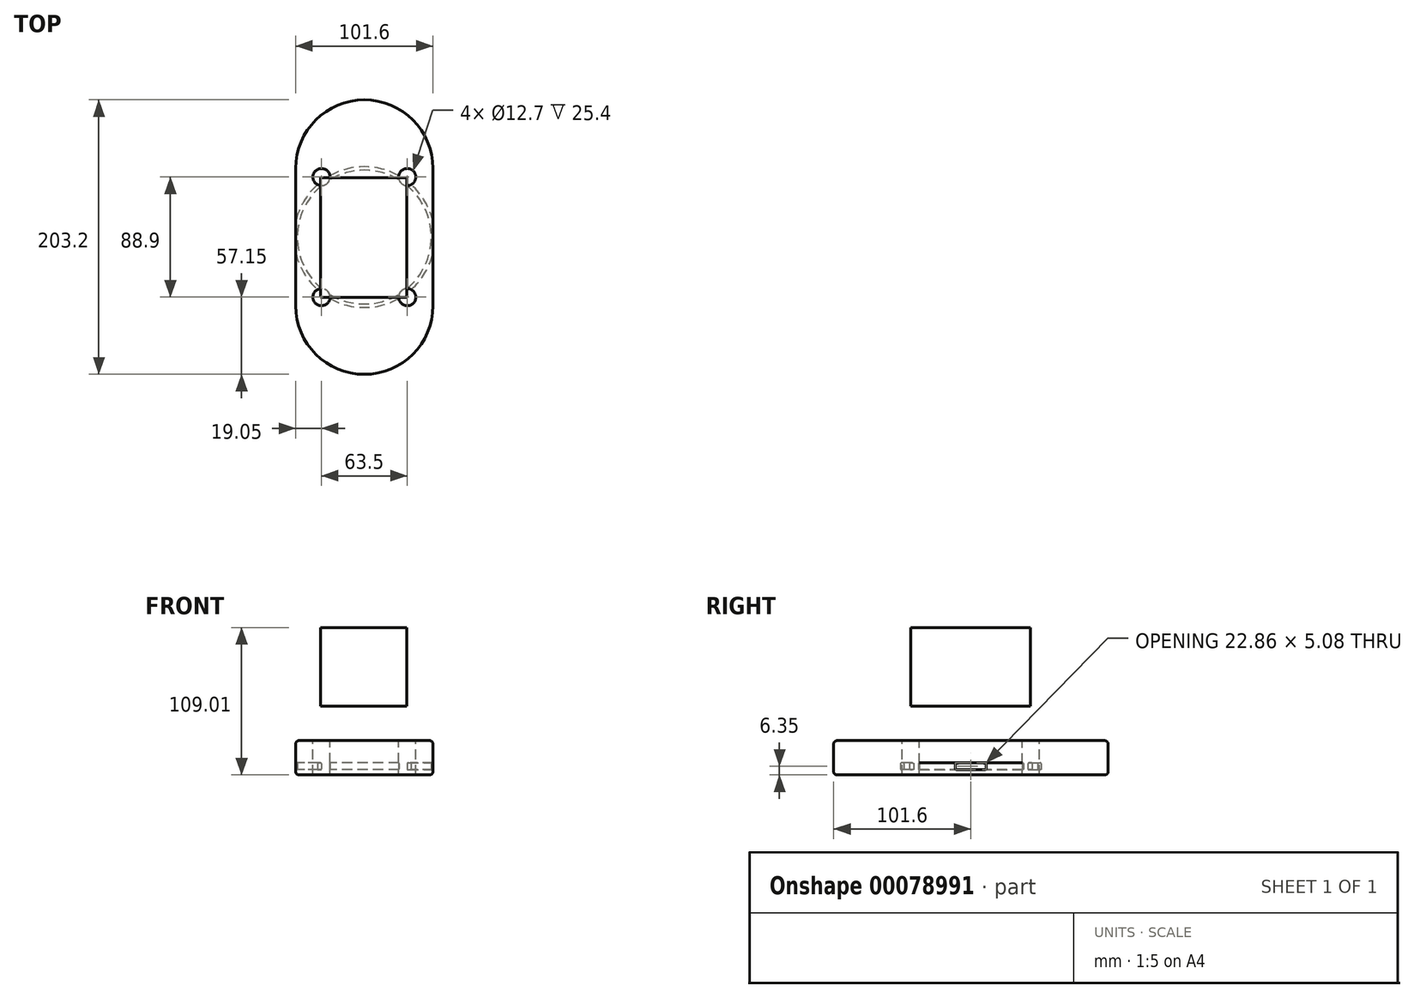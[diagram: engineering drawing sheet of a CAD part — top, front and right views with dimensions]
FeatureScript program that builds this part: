
annotation { "Feature Type Name" : "Feature", "Feature Type Description" : "" }
export const myFeature = defineFeature(function(context is Context, id is Id, definition is map)
    precondition{}
    {
        {
            var Q0;
            Q0=qCreatedBy(makeId("Top.planeOp"),FACE);
            var sketch = newSketch(context, id + "F0", { "sketchPlane" : qUnion([Q0])});
            skLineSegment(sketch, "E0", {"start": v(-50.8, -50.8) * mm, "end": v(-50.8, 50.8) * mm});
            skArc(sketch, "E1", {"start": v(50.8, 50.8) * mm, "mid": v(0, 101.6) * mm, "end": v(-50.8, 50.8) * mm});
            skArc(sketch, "E2", {"start": v(-50.8, -50.8) * mm, "mid": v(0, -101.6) * mm, "end": v(50.8, -50.8) * mm});
            skLineSegment(sketch, "E3", {"start": v(50.8, 50.8) * mm, "end": v(50.8, -50.8) * mm});
            skLineSegment(sketch, "E4", {"start": v(0, 50.8) * mm, "end": v(0, -50.8) * mm, "construction": true});
            skSolve(sketch);
        }
        {
            var Q0;
            Q0=qCreatedBy(makeId("Front.planeOp"),FACE);
            var sketch = newSketch(context, id + "F1", { "sketchPlane" : qUnion([Q0])});
            skLineSegment(sketch, "E5.bottom", {"start": v(51.44, 3.81) * mm, "end": v(50.16, 3.81) * mm});
            skLineSegment(sketch, "E5.top", {"start": v(51.44, 8.89) * mm, "end": v(50.16, 8.89) * mm});
            skLineSegment(sketch, "E5.left", {"start": v(52.07, 4.45) * mm, "end": v(52.07, 8.25) * mm});
            skLineSegment(sketch, "E5.right", {"start": v(49.53, 4.45) * mm, "end": v(49.53, 8.25) * mm});
            skLineSegment(sketch, "E6", {"start": v(50.8, 3.81) * mm, "end": v(50.8, 8.89) * mm, "construction": true});
            skLineSegment(sketch, "E7", {"start": v(52.07, 6.35) * mm, "end": v(49.53, 6.35) * mm, "construction": true});
            skPoint(sketch, "E8.visualSharp", {"position": v(52.07, 8.89) * mm});
            skArc(sketch, "E8.filletArc", {"start": v(52.07, 8.25) * mm, "mid": v(51.88, 8.7) * mm, "end": v(51.44, 8.89) * mm});
            skPoint(sketch, "E9.visualSharp", {"position": v(49.53, 8.9) * mm});
            skArc(sketch, "E9.filletArc", {"start": v(50.16, 8.89) * mm, "mid": v(49.72, 8.7) * mm, "end": v(49.53, 8.25) * mm});
            skPoint(sketch, "E10.visualSharp", {"position": v(49.53, 3.81) * mm});
            skArc(sketch, "E10.filletArc", {"start": v(49.53, 4.45) * mm, "mid": v(49.72, 4) * mm, "end": v(50.16, 3.81) * mm});
            skPoint(sketch, "E11.visualSharp", {"position": v(52.07, 3.81) * mm});
            skArc(sketch, "E11.filletArc", {"start": v(51.44, 3.81) * mm, "mid": v(51.88, 4) * mm, "end": v(52.07, 4.45) * mm});
            skSolve(sketch);
        }
        {
            var Q0;
            Q0 = qSketchRegion(id + "F0", true);
            extrude(context, id + "F2", {"entities" : qUnion([Q0]), "depth" : 25.4 * mm});
        }
        {
            var Q0;
            Q0=makeQuery(id+"F2.opExtrude","CAP_FACE",FACE,{"disambiguationData":[OSD([sQuery(id+"F0.wireOp",EDGE,"E0"),sQuery(id+"F0.wireOp",EDGE,"E1"),sQuery(id+"F0.wireOp",EDGE,"E2"),sQuery(id+"F0.wireOp",EDGE,"E3")])],"isStart":false});
            var sketch = newSketch(context, id + "F3", { "sketchPlane" : qUnion([Q0])});
            skLineSegment(sketch, "E12.bottom", {"start": v(-31.75, 44.45) * mm, "end": v(31.75, 44.45) * mm, "construction": true});
            skLineSegment(sketch, "E12.top", {"start": v(-31.75, -44.45) * mm, "end": v(31.75, -44.45) * mm, "construction": true});
            skLineSegment(sketch, "E12.left", {"start": v(-31.75, 44.45) * mm, "end": v(-31.75, -44.45) * mm, "construction": true});
            skLineSegment(sketch, "E12.right", {"start": v(31.75, 44.45) * mm, "end": v(31.75, -44.45) * mm, "construction": true});
            skCircle(sketch, "E13", {"center": v(-31.75, 44.45) * mm, "radius": 6.35 * mm});
            skCircle(sketch, "E14", {"center": v(31.75, 44.45) * mm, "radius": 6.35 * mm});
            skCircle(sketch, "E15", {"center": v(31.75, -44.45) * mm, "radius": 6.35 * mm});
            skCircle(sketch, "E16", {"center": v(-31.75, -44.45) * mm, "radius": 6.35 * mm});
            skSolve(sketch);
        }
        {
            var Q0;
            Q0 = qSketchRegion(id + "F3", true);
            extrude(context, id + "F4", {"entities" : qUnion([Q0]), "operationType" : NewBodyOperationType.REMOVE, "oppositeDirection" : true, "depth" : 25.4 * mm});
        }
        {
            var Q0;
            Q0=qCreatedBy(makeId("Front.planeOp"),FACE);
            var sketch = newSketch(context, id + "F5", { "sketchPlane" : qUnion([Q0])});
            skLineSegment(sketch, "E17", {"start": v(0, 58.33) * mm, "end": v(0, -58.9) * mm});
            skSolve(sketch);
        }
        {
            var Q0;
            Q0=makeQuery(id+"F1.imprint","IMPRINT",FACE,{"disambiguationData":[TD([[makeQuery(id+"F1.imprint","IMPRINT",EDGE,{"derivedFrom":sQuery(id+"F1.wireOp",EDGE,"E5.bottom")}),-1.0]])]});
            var Q1;
            Q1=sQuery(id+"F5.wireOp",EDGE,"E17");
            revolve(context, id + "F6", {"operationType" : NewBodyOperationType.REMOVE, "entities" : qUnion([Q0]), "axis" : qUnion([Q1]), "revolveType" : RevolveType.FULL, "oppositeDirection" : true});
        }
        {
            var Q0;
            Q0=makeQuery(id+"F2.opExtrude","CAP_EDGE",EDGE,{"disambiguationData":[OSD([sQuery(id+"F0.wireOp",EDGE,"E0")])],"isStart":false});
            var Q1;
            Q1=makeQuery(id+"F2.opExtrude","CAP_EDGE",EDGE,{"disambiguationData":[OSD([sQuery(id+"F0.wireOp",EDGE,"E0")])],"isStart":true});
            var Q2;
            Q2=makeQuery(id+"F2.opExtrude","CAP_EDGE",EDGE,{"disambiguationData":[OSD([sQuery(id+"F0.wireOp",EDGE,"E0")])],"isStart":true});
            fillet(context, id + "F7", {"entities" : qUnion([Q0, Q1, Q2]), "radius" : 2.54 * mm, "tangentPropagation" : true, "allowEdgeOverflow" : false});
        }
        {
            var Q0;
            Q0=qCreatedBy(makeId("Top.planeOp"),FACE);
            var sketch = newSketch(context, id + "F8", { "sketchPlane" : qUnion([Q0])});
            skLineSegment(sketch, "E18.bottom", {"start": v(-32.33, 44.11) * mm, "end": v(31.43, 44.11) * mm});
            skLineSegment(sketch, "E18.top", {"start": v(-32.33, -44.56) * mm, "end": v(31.43, -44.56) * mm});
            skLineSegment(sketch, "E18.left", {"start": v(-32.33, 44.11) * mm, "end": v(-32.33, -44.56) * mm});
            skLineSegment(sketch, "E18.right", {"start": v(31.43, 44.11) * mm, "end": v(31.43, -44.56) * mm});
            skSolve(sketch);
        }
        {
            var Q0;
            Q0 = qSketchRegion(id + "F8", true);
            extrude(context, id + "F9", {"entities" : qUnion([Q0]), "depth" : 109.01 * mm, "hasSecondDirection" : true, "secondDirectionOppositeDirection" : false, "secondDirectionDepth" : 50.8 * mm});
        }
    });
